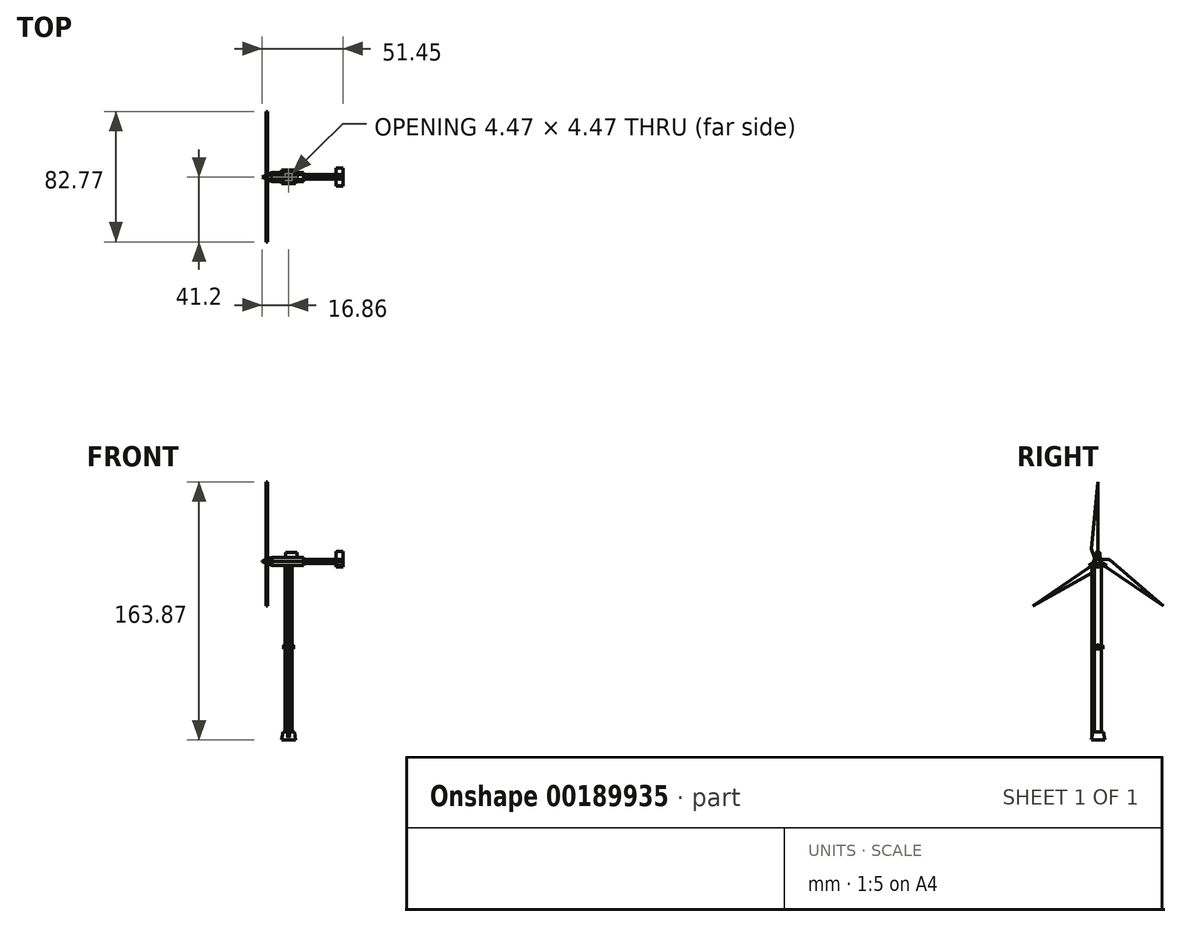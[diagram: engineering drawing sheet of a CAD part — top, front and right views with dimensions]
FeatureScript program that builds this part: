
annotation { "Feature Type Name" : "Feature", "Feature Type Description" : "" }
export const myFeature = defineFeature(function(context is Context, id is Id, definition is map)
    precondition{}
    {
        {
            var Q0;
            Q0=qCreatedBy(makeId("Top.planeOp"),FACE);
            var sketch = newSketch(context, id + "F0", { "sketchPlane" : qUnion([Q0])});
            skCircle(sketch, "E0", {"center": v(0, 0) * mm, "radius": 3.1 * mm});
            skSolve(sketch);
        }
        {
            var Q0;
            Q0 = qSketchRegion(id + "F0", true);
            extrude(context, id + "F1", {"entities" : qUnion([Q0]), "depth" : 1 * mm});
        }
        {
            var Q0;
            Q0=makeQuery(id+"F1.opExtrude","CAP_FACE",FACE,{"disambiguationData":[OSD([sQuery(id+"F0.wireOp",EDGE,"E0")])],"isStart":false});
            var sketch = newSketch(context, id + "F2", { "sketchPlane" : qUnion([Q0])});
            skCircle(sketch, "E1", {"center": v(0, 0) * mm, "radius": 2.23 * mm});
            skSolve(sketch);
        }
        {
            var Q0;
            Q0=makeQuery(id+"F2.imprint","IMPRINT",FACE,{"disambiguationData":[TD([[makeQuery(id+"F2.imprint","IMPRINT",EDGE,{"derivedFrom":sQuery(id+"F2.wireOp",EDGE,"E1")}),1.0]])]});
            extrude(context, id + "F3", {"entities" : qUnion([Q0]), "operationType" : NewBodyOperationType.ADD, "depth" : 45 * mm});
        }
        {
            var Q0;
            Q0=makeQuery(id+"F1.opExtrude","CAP_FACE",FACE,{"disambiguationData":[OSD([sQuery(id+"F0.wireOp",EDGE,"E0")])],"isStart":false});
            var sketch = newSketch(context, id + "F4", { "sketchPlane" : qUnion([Q0])});
            skCircle(sketch, "E2", {"center": v(0, 2.7) * mm, "radius": 0.23 * mm});
            skCircle(sketch, "E3", {"center": v(2.7, 0) * mm, "radius": 0.23 * mm});
            skCircle(sketch, "E4", {"center": v(0, -2.68) * mm, "radius": 0.23 * mm});
            skCircle(sketch, "E5", {"center": v(-2.75, 0) * mm, "radius": 0.28 * mm});
            skSolve(sketch);
        }
        {
            var Q0;
            Q0 = qSketchRegion(id + "F4", true);
            extrude(context, id + "F5", {"entities" : qUnion([Q0]), "operationType" : NewBodyOperationType.ADD, "depth" : 0.3 * mm, "hasSecondDirection" : true, "secondDirectionOppositeDirection" : true, "secondDirectionDepth" : 1.3 * mm});
        }
        {
            var Q0;
            Q0=makeQuery(id+"F5.opExtrude","CAP_FACE",FACE,{"disambiguationData":[OSD([sQuery(id+"F4.wireOp",EDGE,"E5")])],"isStart":true});
            var sketch = newSketch(context, id + "F6", { "sketchPlane" : qUnion([Q0])});
            skCircle(sketch, "E6", {"center": v(0, 0) * mm, "radius": 3.1 * mm});
            skSolve(sketch);
        }
        {
            var Q0;
            Q0 = qSketchRegion(id + "F6", true);
            extrude(context, id + "F7", {"entities" : qUnion([Q0]), "operationType" : NewBodyOperationType.ADD, "depth" : 1 * mm});
        }
        {
            var Q0;
            Q0=makeQuery(id+"F3.opExtrude","CAP_FACE",FACE,{"disambiguationData":[OSD([sQuery(id+"F2.wireOp",EDGE,"E1")])],"isStart":false});
            extrude(context, id + "F8", {"entities" : qUnion([Q0]), "operationType" : NewBodyOperationType.ADD, "depth" : 5 * mm, "hasSecondDirection" : true, "secondDirectionOppositeDirection" : true, "secondDirectionDepth" : 100 * mm});
        }
        {
            var Q0;
            Q0=makeQuery(id+"F8.opExtrude","CAP_FACE",FACE,{"disambiguationData":[OSD([sQuery(id+"F2.wireOp",EDGE,"E1")])],"isStart":true});
            var sketch = newSketch(context, id + "F9", { "sketchPlane" : qUnion([Q0])});
            skLineSegment(sketch, "E7.bottom", {"start": v(-3.46, 3.28) * mm, "end": v(3.65, 3.28) * mm});
            skLineSegment(sketch, "E7.top", {"start": v(-3.46, -3.46) * mm, "end": v(3.65, -3.46) * mm});
            skLineSegment(sketch, "E7.left", {"start": v(-3.46, 3.28) * mm, "end": v(-3.46, -3.46) * mm});
            skLineSegment(sketch, "E7.right", {"start": v(3.65, 3.28) * mm, "end": v(3.65, -3.46) * mm});
            skSolve(sketch);
        }
        {
            var Q0;
            Q0 = qSketchRegion(id + "F9", true);
            extrude(context, id + "F10", {"entities" : qUnion([Q0]), "operationType" : NewBodyOperationType.ADD, "depth" : 5 * mm, "hasDraft" : true, "draftAngle" : 10 * degree});
        }
        {
            var Q0;
            Q0=makeQuery(id+"F8.opExtrude","CAP_FACE",FACE,{"disambiguationData":[OSD([sQuery(id+"F2.wireOp",EDGE,"E1")])],"isStart":false});
            var sketch = newSketch(context, id + "F11", { "sketchPlane" : qUnion([Q0])});
            skCircle(sketch, "E8", {"center": v(0, 0) * mm, "radius": 1.53 * mm});
            skSolve(sketch);
        }
        {
            var Q0;
            Q0=makeQuery(id+"F11.imprint","IMPRINT",FACE,{"disambiguationData":[TD([[makeQuery(id+"F11.imprint","IMPRINT",EDGE,{"derivedFrom":sQuery(id+"F11.wireOp",EDGE,"E8")}),1.0]])]});
            extrude(context, id + "F12", {"entities" : qUnion([Q0]), "operationType" : NewBodyOperationType.ADD, "depth" : 1 * mm});
        }
        {
            var Q0;
            Q0=makeQuery(id+"F12.opExtrude","CAP_FACE",FACE,{"disambiguationData":[OSD([sQuery(id+"F11.wireOp",EDGE,"E8")])],"isStart":false});
            var sketch = newSketch(context, id + "F13", { "sketchPlane" : qUnion([Q0])});
            skLineSegment(sketch, "E9.bottom", {"start": v(0, 0) * mm, "end": v(0.4, 0) * mm});
            skLineSegment(sketch, "E9.top", {"start": v(0, -0.44) * mm, "end": v(0.4, -0.44) * mm});
            skLineSegment(sketch, "E9.left", {"start": v(0, 0) * mm, "end": v(0, -0.44) * mm});
            skLineSegment(sketch, "E9.right", {"start": v(0.4, 0) * mm, "end": v(0.4, -0.44) * mm});
            skLineSegment(sketch, "E10.bottom", {"start": v(0.4, -0.44) * mm, "end": v(-0.41, -0.44) * mm});
            skLineSegment(sketch, "E10.top", {"start": v(0.4, 0) * mm, "end": v(-0.41, 0) * mm});
            skLineSegment(sketch, "E10.left", {"start": v(0.4, -0.44) * mm, "end": v(0.4, 0) * mm});
            skLineSegment(sketch, "E10.right", {"start": v(-0.41, -0.44) * mm, "end": v(-0.41, 0) * mm});
            skSolve(sketch);
        }
        {
            var Q0;
            Q0 = qSketchRegion(id + "F13", true);
            extrude(context, id + "F14", {"entities" : qUnion([Q0]), "operationType" : NewBodyOperationType.ADD, "depth" : 5 * mm});
        }
        {
            var Q0;
            Q0=makeQuery(id+"F14.opExtrude","SWEPT_FACE",FACE,{"disambiguationData":[OSD([sQuery(id+"F13.wireOp",EDGE,"E10.right")])]});
            var sketch = newSketch(context, id + "F15", { "sketchPlane" : qUnion([Q0])});
            skCircle(sketch, "E11.cCircle", {"center": v(0, 54.5) * mm, "radius": 2.5 * mm, "construction": true});
            skLineSegment(sketch, "E11.0", {"start": v(-1.44, 57) * mm, "end": v(1.44, 57) * mm});
            skLineSegment(sketch, "E11.1", {"start": v(1.44, 57) * mm, "end": v(2.89, 54.5) * mm});
            skLineSegment(sketch, "E11.2", {"start": v(2.89, 54.5) * mm, "end": v(1.44, 52) * mm});
            skLineSegment(sketch, "E11.3", {"start": v(1.44, 52) * mm, "end": v(-1.44, 52) * mm});
            skLineSegment(sketch, "E11.4", {"start": v(-1.44, 52) * mm, "end": v(-2.89, 54.5) * mm});
            skLineSegment(sketch, "E11.5", {"start": v(-2.89, 54.5) * mm, "end": v(-1.44, 57) * mm});
            skPoint(sketch, "E11.0.midPoint", {"position": v(0, 57) * mm});
            skSolve(sketch);
        }
        {
            var Q0;
            Q0 = qSketchRegion(id + "F15", true);
            extrude(context, id + "F16", {"entities" : qUnion([Q0]), "operationType" : NewBodyOperationType.ADD, "depth" : 10 * mm, "hasSecondDirection" : true, "secondDirectionOppositeDirection" : true, "secondDirectionDepth" : 15 * mm});
        }
        {
            var Q0;
            Q0=makeQuery(id+"F16.opExtrude","CAP_FACE",FACE,{"disambiguationData":[OSD([sQuery(id+"F15.wireOp",EDGE,"E11.0"),sQuery(id+"F15.wireOp",EDGE,"E11.1"),sQuery(id+"F15.wireOp",EDGE,"E11.2"),sQuery(id+"F15.wireOp",EDGE,"E11.3"),sQuery(id+"F15.wireOp",EDGE,"E11.4"),sQuery(id+"F15.wireOp",EDGE,"E11.5")])],"isStart":false});
            extrude(context, id + "F17", {"entities" : qUnion([Q0]), "operationType" : NewBodyOperationType.ADD, "depth" : 3 * mm, "hasDraft" : true, "draftAngle" : 15 * degree, "draftPullDirection" : true});
        }
        {
            var Q0;
            Q0=makeQuery(id+"F17.opExtrude","CAP_FACE",FACE,{"disambiguationData":[OSD([sQuery(id+"F15.wireOp",EDGE,"E11.0"),sQuery(id+"F15.wireOp",EDGE,"E11.1"),sQuery(id+"F15.wireOp",EDGE,"E11.2"),sQuery(id+"F15.wireOp",EDGE,"E11.3"),sQuery(id+"F15.wireOp",EDGE,"E11.4"),sQuery(id+"F15.wireOp",EDGE,"E11.5")])],"isStart":false});
            var sketch = newSketch(context, id + "F18", { "sketchPlane" : qUnion([Q0])});
            skCircle(sketch, "E12", {"center": v(0, 54.5) * mm, "radius": 1.41 * mm});
            skPoint(sketch, "E12.centerSnap0", {"position": v(0, 52.8) * mm});
            skSolve(sketch);
        }
        {
            var Q0;
            Q0=makeQuery(id+"F18.imprint","IMPRINT",FACE,{"disambiguationData":[TD([[makeQuery(id+"F18.imprint","IMPRINT",EDGE,{"derivedFrom":sQuery(id+"F18.wireOp",EDGE,"E12")}),1.0]])]});
            extrude(context, id + "F19", {"entities" : qUnion([Q0]), "operationType" : NewBodyOperationType.ADD, "depth" : 1 * mm});
        }
        {
            var Q0;
            Q0=makeQuery(id+"F19.opExtrude","CAP_FACE",FACE,{"disambiguationData":[OSD([sQuery(id+"F18.wireOp",EDGE,"E12")])],"isStart":false});
            var sketch = newSketch(context, id + "F20", { "sketchPlane" : qUnion([Q0])});
            skLineSegment(sketch, "E13", {"start": v(0, 54.5) * mm, "end": v(41.2, 26.1) * mm});
            skLineSegment(sketch, "E14", {"start": v(41.2, 26.1) * mm, "end": v(2.8, 47.63) * mm});
            skLineSegment(sketch, "E15", {"start": v(2.8, 47.63) * mm, "end": v(0, 53.09) * mm});
            skLineSegment(sketch, "E16", {"start": v(0, 53.09) * mm, "end": v(0, 54.5) * mm});
            skLineSegment(sketch, "E17", {"start": v(0, 54.5) * mm, "end": v(0, 104.87) * mm});
            skLineSegment(sketch, "E18", {"start": v(0, 104.87) * mm, "end": v(3.93, 62.43) * mm});
            skLineSegment(sketch, "E19", {"start": v(3.93, 62.43) * mm, "end": v(1.48, 54.5) * mm});
            skLineSegment(sketch, "E20", {"start": v(1.48, 54.5) * mm, "end": v(0, 54.5) * mm});
            skLineSegment(sketch, "E21", {"start": v(0, 54.5) * mm, "end": v(-41.57, 26.1) * mm});
            skLineSegment(sketch, "E22", {"start": v(-41.57, 26.1) * mm, "end": v(-7.2, 55.57) * mm});
            skLineSegment(sketch, "E23", {"start": v(-7.2, 55.57) * mm, "end": v(-0.92, 55.57) * mm});
            skLineSegment(sketch, "E24", {"start": v(-0.92, 55.57) * mm, "end": v(0, 54.5) * mm});
            skSolve(sketch);
        }
        {
            var Q0;
            Q0 = qSketchRegion(id + "F20", true);
            extrude(context, id + "F21", {"entities" : qUnion([Q0]), "operationType" : NewBodyOperationType.ADD, "oppositeDirection" : true, "depth" : 1 * mm});
        }
        {
            var Q0;
            Q0=makeQuery(id+"F21.boolean.opBoolean","MERGE",FACE,{"derivedFrom":[makeQuery(id+"F19.opExtrude","CAP_FACE",FACE,{"disambiguationData":[OSD([sQuery(id+"F18.wireOp",EDGE,"E12")])],"isStart":false}),makeQuery(id+"F21.opExtrude","CAP_FACE",FACE,{"disambiguationData":[OSD([sQuery(id+"F20.wireOp",EDGE,"E13"),sQuery(id+"F20.wireOp",EDGE,"E14"),sQuery(id+"F20.wireOp",EDGE,"E15"),sQuery(id+"F20.wireOp",EDGE,"E16")])],"isStart":true}),makeQuery(id+"F21.opExtrude","CAP_FACE",FACE,{"disambiguationData":[OSD([sQuery(id+"F20.wireOp",EDGE,"E17"),sQuery(id+"F20.wireOp",EDGE,"E18"),sQuery(id+"F20.wireOp",EDGE,"E19"),sQuery(id+"F20.wireOp",EDGE,"E20")])],"isStart":true}),makeQuery(id+"F21.opExtrude","CAP_FACE",FACE,{"disambiguationData":[OSD([sQuery(id+"F20.wireOp",EDGE,"E21"),sQuery(id+"F20.wireOp",EDGE,"E22"),sQuery(id+"F20.wireOp",EDGE,"E23"),sQuery(id+"F20.wireOp",EDGE,"E24")])],"isStart":true})]});
            var sketch = newSketch(context, id + "F22", { "sketchPlane" : qUnion([Q0])});
            skCircle(sketch, "E25", {"center": v(0, 54.5) * mm, "radius": 1.41 * mm});
            skSolve(sketch);
        }
        {
            var Q0;
            {var subQ0=sQuery(id+"F22.wireOp",EDGE,"E25");var subQ4=makeQuery(id+"F22.imprint","INTERSECT",VERTEX,{"derivedFrom":[makeQuery(id+"F21.opExtrude","CAP_EDGE",EDGE,{"disambiguationData":[OSD([sQuery(id+"F20.wireOp",EDGE,"E17")])],"isStart":true}),subQ0]});Q0=makeQuery(id+"F22.imprint","IMPRINT",FACE,{"disambiguationData":[TD([[makeQuery(id+"F22.imprint","IMPRINT",EDGE,{"disambiguationData":[TD([[subQ4,1.0]])],"derivedFrom":subQ0}),1.0]])]});}
            extrude(context, id + "F23", {"entities" : qUnion([Q0]), "operationType" : NewBodyOperationType.ADD, "depth" : 3 * mm, "hasDraft" : true, "draftAngle" : 30 * degree, "draftPullDirection" : true});
        }
        {
            var Q0;
            Q0=makeQuery(id+"F16.boolean.opBoolean","MERGE",FACE,{"derivedFrom":[makeQuery(id+"F14.opExtrude","CAP_FACE",FACE,{"disambiguationData":[OSD([sQuery(id+"F13.wireOp",EDGE,"E10.bottom"),sQuery(id+"F13.wireOp",EDGE,"E10.top"),sQuery(id+"F13.wireOp",EDGE,"E10.left"),sQuery(id+"F13.wireOp",EDGE,"E10.right")])],"isStart":false}),makeQuery(id+"F16.opExtrude","SWEPT_FACE",FACE,{"disambiguationData":[OSD([sQuery(id+"F15.wireOp",EDGE,"E11.0")])]})]});
            var sketch = newSketch(context, id + "F24", { "sketchPlane" : qUnion([Q0])});
            skLineSegment(sketch, "E26.bottom", {"start": v(5.26, 1.44) * mm, "end": v(-2, 1.44) * mm});
            skLineSegment(sketch, "E26.top", {"start": v(5.26, -1.44) * mm, "end": v(-2, -1.44) * mm});
            skLineSegment(sketch, "E26.left", {"start": v(5.26, 1.44) * mm, "end": v(5.26, -1.44) * mm});
            skLineSegment(sketch, "E26.right", {"start": v(-2, 1.44) * mm, "end": v(-2, -1.44) * mm});
            skSolve(sketch);
        }
        {
            var Q0;
            Q0=makeQuery(id+"F24.imprint","IMPRINT",FACE,{"disambiguationData":[TD([[makeQuery(id+"F24.imprint","IMPRINT",EDGE,{"derivedFrom":sQuery(id+"F24.wireOp",EDGE,"E26.bottom")}),-1.0]])]});
            extrude(context, id + "F25", {"entities" : qUnion([Q0]), "operationType" : NewBodyOperationType.ADD, "depth" : 3 * mm});
        }
        {
            var Q0;
            Q0=makeQuery(id+"F16.opExtrude","CAP_FACE",FACE,{"disambiguationData":[OSD([sQuery(id+"F15.wireOp",EDGE,"E11.0"),sQuery(id+"F15.wireOp",EDGE,"E11.1"),sQuery(id+"F15.wireOp",EDGE,"E11.2"),sQuery(id+"F15.wireOp",EDGE,"E11.3"),sQuery(id+"F15.wireOp",EDGE,"E11.4"),sQuery(id+"F15.wireOp",EDGE,"E11.5")])],"isStart":true});
            extrude(context, id + "F26", {"entities" : qUnion([Q0]), "operationType" : NewBodyOperationType.REMOVE, "oppositeDirection" : true, "depth" : 5 * mm});
        }
        {
            var Q0;
            Q0=makeQuery(id+"F26.boolean.opBoolean","COPY",FACE,{"derivedFrom":makeQuery(id+"F26.opExtrude","CAP_FACE",FACE,{"disambiguationData":[OSD([sQuery(id+"F15.wireOp",EDGE,"E11.0"),sQuery(id+"F15.wireOp",EDGE,"E11.1"),sQuery(id+"F15.wireOp",EDGE,"E11.2"),sQuery(id+"F15.wireOp",EDGE,"E11.3"),sQuery(id+"F15.wireOp",EDGE,"E11.4"),sQuery(id+"F15.wireOp",EDGE,"E11.5")])],"isStart":false})});
            var sketch = newSketch(context, id + "F27", { "sketchPlane" : qUnion([Q0])});
            skCircle(sketch, "E27.cCircle", {"center": v(0, 54.5) * mm, "radius": 1.23 * mm, "construction": true});
            skPoint(sketch, "E27.cCircle.centerSnap0", {"position": v(0, 52) * mm});
            skPoint(sketch, "E27.cCircle.perimeterSnap0", {"position": v(0, 52) * mm});
            skLineSegment(sketch, "E27.0", {"start": v(-0.7, 55.73) * mm, "end": v(0.7, 55.73) * mm});
            skLineSegment(sketch, "E27.1", {"start": v(0.7, 55.73) * mm, "end": v(1.42, 54.5) * mm});
            skLineSegment(sketch, "E27.2", {"start": v(1.42, 54.5) * mm, "end": v(0.7, 53.27) * mm});
            skLineSegment(sketch, "E27.3", {"start": v(0.7, 53.27) * mm, "end": v(-0.7, 53.27) * mm});
            skLineSegment(sketch, "E27.4", {"start": v(-0.7, 53.27) * mm, "end": v(-1.42, 54.5) * mm});
            skLineSegment(sketch, "E27.5", {"start": v(-1.42, 54.5) * mm, "end": v(-0.7, 55.73) * mm});
            skPoint(sketch, "E27.0.midPoint", {"position": v(0, 55.73) * mm});
            skPoint(sketch, "E27.0.midPoint.positionSnap0", {"position": v(0, 52) * mm});
            skSolve(sketch);
        }
        {
            var Q0;
            Q0 = qSketchRegion(id + "F27", true);
            extrude(context, id + "F28", {"entities" : qUnion([Q0]), "operationType" : NewBodyOperationType.ADD, "depth" : 25 * mm});
        }
        {
            var Q0;
            Q0=makeQuery(id+"F28.opExtrude","SWEPT_FACE",FACE,{"disambiguationData":[OSD([sQuery(id+"F27.wireOp",EDGE,"E27.0")])]});
            var sketch = newSketch(context, id + "F29", { "sketchPlane" : qUnion([Q0])});
            skLineSegment(sketch, "E28.bottom", {"start": v(34.59, 0.7) * mm, "end": v(30.1, 0.7) * mm});
            skLineSegment(sketch, "E28.top", {"start": v(34.59, -0.7) * mm, "end": v(30.1, -0.7) * mm});
            skLineSegment(sketch, "E28.left", {"start": v(34.59, 0.7) * mm, "end": v(34.59, -0.7) * mm});
            skLineSegment(sketch, "E28.right", {"start": v(30.1, 0.7) * mm, "end": v(30.1, -0.7) * mm});
            skSolve(sketch);
        }
        {
            var Q0;
            Q0 = qSketchRegion(id + "F29", true);
            extrude(context, id + "F30", {"entities" : qUnion([Q0]), "operationType" : NewBodyOperationType.ADD, "depth" : 5 * mm});
        }
        {
            var Q0;
            Q0=makeQuery(id+"F28.opExtrude","SWEPT_FACE",FACE,{"disambiguationData":[OSD([sQuery(id+"F27.wireOp",EDGE,"E27.2")])]});
            var sketch = newSketch(context, id + "F31", { "sketchPlane" : qUnion([Q0])});
            skLineSegment(sketch, "E29.bottom", {"start": v(-34.59, 46.49) * mm, "end": v(-30.08, 46.49) * mm});
            skLineSegment(sketch, "E29.top", {"start": v(-34.59, 47.9) * mm, "end": v(-30.08, 47.9) * mm});
            skLineSegment(sketch, "E29.left", {"start": v(-34.59, 46.49) * mm, "end": v(-34.59, 47.9) * mm});
            skLineSegment(sketch, "E29.right", {"start": v(-30.08, 46.49) * mm, "end": v(-30.08, 47.9) * mm});
            skSolve(sketch);
        }
        {
            var Q0;
            Q0 = qSketchRegion(id + "F31", true);
            extrude(context, id + "F32", {"entities" : qUnion([Q0]), "operationType" : NewBodyOperationType.ADD, "depth" : 5 * mm});
        }
        {
            var Q0;
            Q0=makeQuery(id+"F28.opExtrude","SWEPT_FACE",FACE,{"disambiguationData":[OSD([sQuery(id+"F27.wireOp",EDGE,"E27.4")])]});
            var sketch = newSketch(context, id + "F33", { "sketchPlane" : qUnion([Q0])});
            skLineSegment(sketch, "E30.bottom", {"start": v(34.59, 47.9) * mm, "end": v(30.07, 47.9) * mm});
            skLineSegment(sketch, "E30.top", {"start": v(34.59, 46.49) * mm, "end": v(30.07, 46.49) * mm});
            skLineSegment(sketch, "E30.left", {"start": v(34.59, 47.9) * mm, "end": v(34.59, 46.49) * mm});
            skLineSegment(sketch, "E30.right", {"start": v(30.07, 47.9) * mm, "end": v(30.07, 46.49) * mm});
            skSolve(sketch);
        }
        {
            var Q0;
            Q0=makeQuery(id+"F33.imprint","IMPRINT",FACE,{"disambiguationData":[TD([[makeQuery(id+"F33.imprint","IMPRINT",EDGE,{"derivedFrom":sQuery(id+"F33.wireOp",EDGE,"E30.bottom")}),1.0]])]});
            extrude(context, id + "F34", {"entities" : qUnion([Q0]), "operationType" : NewBodyOperationType.ADD, "depth" : 5 * mm});
        }
        {
            var Q0;
            Q0=makeQuery(id+"F8.opExtrude","CAP_FACE",FACE,{"disambiguationData":[OSD([sQuery(id+"F2.wireOp",EDGE,"E1")])],"isStart":false});
            var sketch = newSketch(context, id + "F35", { "sketchPlane" : qUnion([Q0])});
            skLineSegment(sketch, "E31.bottom", {"start": v(-0.51, -1.8) * mm, "end": v(-0.31, -1.8) * mm});
            skLineSegment(sketch, "E31.top", {"start": v(-0.51, -3.86) * mm, "end": v(-0.31, -3.86) * mm});
            skLineSegment(sketch, "E31.left", {"start": v(-0.51, -1.8) * mm, "end": v(-0.51, -3.86) * mm});
            skLineSegment(sketch, "E31.right", {"start": v(-0.31, -1.8) * mm, "end": v(-0.31, -3.86) * mm});
            skLineSegment(sketch, "E32.bottom", {"start": v(0.37, -1.8) * mm, "end": v(0.58, -1.8) * mm});
            skLineSegment(sketch, "E32.top", {"start": v(0.37, -3.86) * mm, "end": v(0.58, -3.86) * mm});
            skLineSegment(sketch, "E32.left", {"start": v(0.37, -1.8) * mm, "end": v(0.37, -3.86) * mm});
            skLineSegment(sketch, "E32.right", {"start": v(0.58, -1.8) * mm, "end": v(0.58, -3.86) * mm});
            skSolve(sketch);
        }
        {
            var Q0;
            Q0 = qSketchRegion(id + "F35", true);
            extrude(context, id + "F36", {"entities" : qUnion([Q0]), "operationType" : NewBodyOperationType.ADD, "depth" : 0.3 * mm});
        }
        {
            var Q0;
            Q0=makeQuery(id+"F36.opExtrude","CAP_FACE",FACE,{"disambiguationData":[OSD([sQuery(id+"F35.wireOp",EDGE,"E32.bottom"),sQuery(id+"F35.wireOp",EDGE,"E32.top"),sQuery(id+"F35.wireOp",EDGE,"E32.left"),sQuery(id+"F35.wireOp",EDGE,"E32.right")])],"isStart":true});
            var sketch = newSketch(context, id + "F37", { "sketchPlane" : qUnion([Q0])});
            skLineSegment(sketch, "E33.bottom", {"start": v(0.58, 3.86) * mm, "end": v(0.37, 3.86) * mm});
            skLineSegment(sketch, "E33.top", {"start": v(0.58, 3.66) * mm, "end": v(0.37, 3.66) * mm});
            skLineSegment(sketch, "E33.left", {"start": v(0.58, 3.86) * mm, "end": v(0.58, 3.66) * mm});
            skLineSegment(sketch, "E33.right", {"start": v(0.37, 3.86) * mm, "end": v(0.37, 3.66) * mm});
            skLineSegment(sketch, "E34.bottom", {"start": v(-0.32, 3.86) * mm, "end": v(-0.52, 3.86) * mm});
            skLineSegment(sketch, "E34.top", {"start": v(-0.32, 3.66) * mm, "end": v(-0.52, 3.66) * mm});
            skLineSegment(sketch, "E34.left", {"start": v(-0.32, 3.86) * mm, "end": v(-0.32, 3.66) * mm});
            skLineSegment(sketch, "E34.right", {"start": v(-0.52, 3.86) * mm, "end": v(-0.52, 3.66) * mm});
            skSolve(sketch);
        }
        {
            var Q0;
            Q0 = qSketchRegion(id + "F37", true);
            extrude(context, id + "F38", {"entities" : qUnion([Q0]), "operationType" : NewBodyOperationType.ADD, "depth" : 110 * mm});
        }
    });
